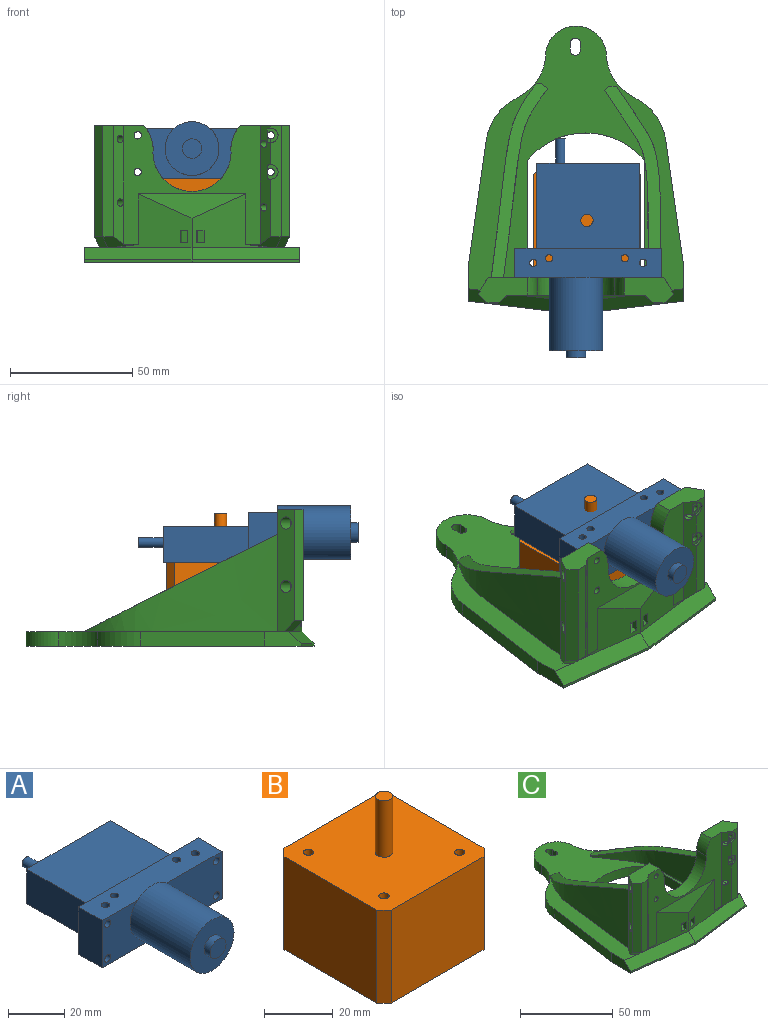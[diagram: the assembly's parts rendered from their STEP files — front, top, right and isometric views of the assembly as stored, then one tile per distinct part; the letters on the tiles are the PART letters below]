
ASSEMBLY  parts=3 mates=2
PART A: 25 faces, bbox 60x89.8x23.3 mm
  f0: plane 20.5x11.8mm, normal (1,0,0), area 241.9mm2, adj f1,f7,f8,f9
  f1: plane 60x20.5mm, normal (0,1,0), area 571.7mm2, adj f0,f2,f8,f9,f10,f11,f12,f13
  f2: plane 20.5x11.8mm, normal (-1,0,0), area 241.9mm2, adj f1,f7,f8,f9
  f3: cylinder r=1.5mm len=20.5mm, axis (0,0,-1), area 193.2mm2, adj f8,f9
  f4: cylinder r=1.5mm len=20.5mm, axis (0,0,-1), area 193.2mm2, adj f8,f9
  f5: cylinder r=1.5mm len=20.5mm, axis (0,0,-1), area 193.2mm2, adj f8,f9
  f6: cylinder r=1.5mm len=20.5mm, axis (0,0,-1), area 193.2mm2, adj f8,f9
  f7: plane 60x20.5mm, normal (0,-1,0), area 850.3mm2, adj f0,f2,f8,f9,f10,f11,f12,f13
  f8: plane 60x11.8mm, normal (0,0,1), area 679.7mm2, adj f0,f1,f2,f3,f4,f5,f6,f7
  f9: plane 60x46.8mm, normal (0,0,-1), area 2149.7mm2, adj f0,f1,f2,f3,f4,f5,f6,f7
  f10: cylinder r=1.5mm len=11.8mm, axis (0,1,0), area 111.2mm2, adj f1,f7
  f11: cylinder r=1.5mm len=11.8mm, axis (0,1,0), area 111.2mm2, adj f1,f7
  f12: cylinder r=1.5mm len=11.8mm, axis (0,1,0), area 111.2mm2, adj f1,f7
  f13: cylinder r=1.5mm len=11.8mm, axis (0,1,0), area 111.2mm2, adj f1,f7
  f14: plane 14.75x2.84mm, normal (0,1,0), area 28.7mm2, adj f8,f15
  f15: cylinder r=11mm len=30mm, axis (0,1,0), area 2073.5mm2, adj f7,f14,f16
  f16: plane 22x22mm, normal (0,-1,0), area 329.9mm2, adj f15,f17
  f17: cylinder r=4mm len=8mm, axis (0,1,0), area 75.4mm2, adj f16,f18
  f18: plane 8x8mm, normal (0,-1,0), area 50.3mm2, adj f17
  f19: plane 35x15mm, normal (1,0,0), area 525mm2, adj f1,f9,f21,f22
  f20: plane 35x15mm, normal (-1,0,0), area 525mm2, adj f1,f9,f21,f22
  f21: plane 42x35mm, normal (0,0,1), area 1470mm2, adj f1,f19,f20,f22
  f22: plane 42x15mm, normal (0,1,0), area 617.4mm2, adj f9,f19,f20,f21,f23
  f23: cylinder r=2mm len=10mm, axis (0,-1,0), area 125.7mm2, adj f22,f24
  f24: plane 4x4mm, normal (0,1,0), area 12.6mm2, adj f23
PART B: 20 faces, bbox 44x44x53 mm
  f0: plane 38x33mm, normal (1,0,0), area 1254mm2, adj f4,f5,f10,f11
  f1: plane 38x33mm, normal (0,1,0), area 1254mm2, adj f4,f5,f9,f11
  f2: plane 38x33mm, normal (-1,0,0), area 1254mm2, adj f4,f5,f8,f9
  f3: plane 38x33mm, normal (0,-1,0), area 1254mm2, adj f4,f5,f8,f10
  f4: plane 44x44mm, normal (0,0,1), area 1870.1mm2, adj f0,f1,f2,f3,f6,f8,f9,f10
  f5: plane 44x44mm, normal (0,0,-1), area 1918mm2, adj f0,f1,f2,f3,f8,f9,f10,f11
  f6: cylinder r=2.5mm len=20mm, axis (0,0,-1), area 314.2mm2, adj f4,f7
  f7: plane 5x5mm, normal (0,0,1), area 19.6mm2, adj f6
  f8: plane 33x3mm, normal (-0.71,-0.71,0), area 140mm2, adj f2,f3,f4,f5
  f9: plane 33x3mm, normal (-0.71,0.71,0), area 140mm2, adj f1,f2,f4,f5
  f10: plane 33x3mm, normal (0.71,-0.71,0), area 140mm2, adj f0,f3,f4,f5
  f11: plane 33x3mm, normal (0.71,0.71,0), area 140mm2, adj f0,f1,f4,f5
  f12: cylinder r=1.5mm len=10mm, axis (0,0,1), area 94.2mm2, adj f4,f13
  f13: plane 3x3mm, normal (0,0,1), area 7.1mm2, adj f12
  f14: cylinder r=1.5mm len=10mm, axis (0,0,1), area 94.2mm2, adj f4,f15
  f15: plane 3x3mm, normal (0,0,1), area 7.1mm2, adj f14
  f16: cylinder r=1.5mm len=10mm, axis (0,0,1), area 94.2mm2, adj f4,f17
  f17: plane 3x3mm, normal (0,0,1), area 7.1mm2, adj f16
  f18: cylinder r=1.5mm len=10mm, axis (0,0,1), area 94.2mm2, adj f4,f19
  f19: plane 3x3mm, normal (0,0,1), area 7.1mm2, adj f18
PART C: 82 faces, bbox 88.2x118.2x56.2 mm
  f0: cylinder r=1.5mm len=9.5mm, axis (0,1,0), area 82.8mm2, adj f14,f60,f61,f79
  f1: plane 45.5x4.5mm, normal (0,-1,0), area 173.5mm2, adj f39,f40,f42,f43,f78,f80
  f2: cylinder r=1.5mm len=9.5mm, axis (0,1,0), area 89.5mm2, adj f14,f81
  f3: plane 32.81x22mm, normal (0.12,-0.99,0), area 369.7mm2, adj f30,f31,f38,f43,f47,f70,f71,f73
  f4: extruded ~77.41x40mm, area 1610mm2, adj f5,f7,f14,f69
  f5: plane 2.52x1.91mm, normal (0.6,0.8,0), area 1.5mm2, adj f4,f7,f69
  f6: extruded ~79.32x40mm, area 1608.4mm2, adj f7,f14,f69
  f7: plane 108.75x88mm, normal (0,0,1), area 3048.4mm2, adj f4,f5,f6,f9,f10,f11,f12,f13
  f8: plane 20.17x10.5mm, normal (0,0,1), area 159.1mm2, adj f14,f34,f35,f36,f37,f38,f52
  f9: plane 6x2.8mm, normal (-1,0,0), area 16.8mm2, adj f7,f10,f27,f28
  f10: cylinder r=2.1mm len=6mm, axis (0,0,-1), area 39.6mm2, adj f7,f9,f11,f28
  f11: plane 6x2.8mm, normal (1,0,0), area 16.8mm2, adj f7,f10,f27,f28
  f12: cylinder r=31.33mm len=48mm, axis (0,0,-1), area 328.1mm2, adj f7,f13,f25,f28
  f13: plane 48x6mm, normal (-1,0,0), area 288mm2, adj f7,f12,f14,f28
  f14: plane 72.02x56.02mm, normal (0,1,0), area 2746.9mm2, adj f0,f2,f4,f6,f7,f8,f13,f25
  f15: plane 50.8x7.22mm, normal (0.99,0.14,0), area 307.9mm2, adj f7,f16,f26,f28
  f16: cylinder r=23.08mm len=17.52mm, axis (0,0,-1), area 135.4mm2, adj f7,f15,f17,f28
  f17: cylinder r=20.78mm len=16.02mm, axis (0,0,-1), area 123.4mm2, adj f7,f16,f18,f28
  f18: cylinder r=12.5mm len=25mm, axis (0,0,-1), area 245.8mm2, adj f7,f17,f19,f28
  f19: cylinder r=20.78mm len=16.02mm, axis (0,0,-1), area 123.4mm2, adj f7,f18,f20,f28
  f20: cylinder r=23.08mm len=17.52mm, axis (0,0,-1), area 135.4mm2, adj f7,f19,f21,f28
  f21: plane 50.8x7.22mm, normal (-0.99,0.14,0), area 307.9mm2, adj f7,f20,f22,f28
  f22: plane 15x6mm, normal (-1,0,0), area 77.4mm2, adj f7,f21,f23,f28,f29
  f23: plane 44x5.32mm, normal (-0.12,-0.99,0), area 44.3mm2, adj f22,f24,f28,f29
  f24: plane 44x5.32mm, normal (0.12,-0.99,0), area 44.3mm2, adj f23,f26,f28,f30
  f25: plane 48x6mm, normal (1,0,0), area 288mm2, adj f7,f12,f14,f28
  f26: plane 15x6mm, normal (1,0,0), area 77.4mm2, adj f7,f15,f24,f28,f30
  f27: cylinder r=2.1mm len=6mm, axis (0,0,-1), area 39.6mm2, adj f7,f9,f11,f28
  f28: plane 118x88mm, normal (0,0,-1), area 4882.9mm2, adj f9,f10,f11,f12,f13,f14,f15,f16
  f29: plane 44x10.35mm, normal (-0.08,-0.7,0.71), area 313.4mm2, adj f7,f22,f23,f30,f31,f32
  f30: plane 44x10.35mm, normal (0.08,-0.7,0.71), area 313.4mm2, adj f3,f7,f24,f26,f29,f33
  f31: plane 32.81x22mm, normal (-0.12,-0.99,0), area 370.2mm2, adj f3,f29,f38,f45,f47,f72,f73,f74
  f32: plane 2.04x0.25mm, normal (0,0,-1), area 0.2mm2, adj f29,f45,f46
  f33: plane 2.04x0.25mm, normal (0,0,-1), area 0.2mm2, adj f30,f43,f44
  f34: plane 50x6.93mm, normal (-0.87,0.5,0), area 350.2mm2, adj f7,f8,f14,f35,f46,f55,f58
  f35: plane 45.5x3.57mm, normal (-0.71,-0.7,0), area 227.5mm2, adj f8,f34,f36,f46
  f36: plane 45.5x4.5mm, normal (0,-1,0), area 204.7mm2, adj f8,f35,f37,f45
  f37: plane 48.7x4mm, normal (0.62,-0.78,0), area 226.1mm2, adj f8,f36,f38,f45,f53,f56
  f38: plane 56x48.7mm, normal (0,-1,0), area 1024.3mm2, adj f3,f8,f31,f37,f39,f42,f43,f45
  f39: plane 48.95x4.25mm, normal (-0.62,-0.78,0), area 207.8mm2, adj f1,f38,f42,f43,f59,f62,f78,f79
  f40: plane 45.5x3.57mm, normal (0.71,-0.7,0), area 227.5mm2, adj f1,f41,f42,f44
  f41: plane 50x6.93mm, normal (0.87,0.5,0), area 350.2mm2, adj f7,f14,f40,f42,f44,f61,f64
  f42: plane 20.17x10.5mm, normal (0,0,1), area 159.1mm2, adj f1,f14,f38,f39,f40,f41,f51
  f43: plane 14.46x4.5mm, normal (0,-0.71,-0.71), area 40.1mm2, adj f1,f3,f33,f38,f39,f44
  f44: plane 7.62x5.39mm, normal (0.5,-0.49,-0.71), area 29.8mm2, adj f7,f33,f40,f41,f43
  f45: plane 14.46x4.5mm, normal (0,-0.71,-0.71), area 40.1mm2, adj f31,f32,f36,f37,f38,f46
  f46: plane 7.62x5.39mm, normal (-0.5,-0.49,-0.71), area 29.8mm2, adj f7,f32,f34,f35,f45
  f47: plane 44.09x9.94mm, normal (0,-0.97,0.26), area 226.9mm2, adj f3,f31,f38
  f48: cylinder r=1.5mm len=7.3mm, axis (0,1,0), area 68.8mm2, adj f14,f38
  f49: cylinder r=1.5mm len=7.3mm, axis (0,1,0), area 68.8mm2, adj f14,f38
  f50: cylinder r=16mm len=32mm, axis (0,1,0), area 390.3mm2, adj f14,f38,f51,f52
  f51: cylinder r=14mm len=9.4mm, axis (0,1,0), area 76.1mm2, adj f14,f38,f42,f50
  f52: cylinder r=14mm len=9.4mm, axis (0,1,0), area 76.1mm2, adj f8,f14,f38,f50
  f53: cylinder r=1.5mm len=3.86mm, axis (-0.87,0.5,0), area 18.1mm2, adj f37,f54
  f54: plane 5x4.33mm, normal (-0.87,0.5,0), area 12.6mm2, adj f53,f55
  f55: cylinder r=2.5mm len=9.43mm, axis (-0.87,0.5,0), area 125.7mm2, adj f34,f54
  f56: cylinder r=1.5mm len=3.86mm, axis (-0.87,0.5,0), area 18.1mm2, adj f37,f57
  f57: plane 5x4.33mm, normal (-0.87,0.5,0), area 12.6mm2, adj f56,f58
  f58: cylinder r=2.5mm len=9.43mm, axis (-0.87,0.5,0), area 125.7mm2, adj f34,f57
  f59: cylinder r=1.5mm len=3.85mm, axis (0.87,0.5,0), area 18.1mm2, adj f39,f60
  f60: plane 5.09x4.42mm, normal (0.87,0.5,0), area 12.4mm2, adj f0,f59,f61,f78,f79
  f61: cylinder r=2.5mm len=9.43mm, axis (0.87,0.5,0), area 119.2mm2, adj f0,f41,f60,f78,f79
  f62: cylinder r=1.5mm len=3.85mm, axis (0.87,0.5,0), area 18.1mm2, adj f39,f63
  f63: plane 5x4.33mm, normal (0.87,0.5,0), area 12.6mm2, adj f62,f64
  f64: cylinder r=2.5mm len=9.43mm, axis (0.87,0.5,0), area 125.7mm2, adj f41,f63
  f65: extruded ~76.59x27mm, area 1079mm2, adj f7,f14,f67,f68
  f66: extruded ~78.32x27mm, area 1076.6mm2, adj f7,f14,f68
  f67: plane 1.73x1.58mm, normal (-0.74,0.67,0), area 0.7mm2, adj f7,f65,f68
  f68: plane 78.32x27mm, normal (0,0.33,0.95), area 437.4mm2, adj f7,f14,f65,f66,f67
  f69: plane 79.32x40mm, normal (0,0.45,0.89), area 459.9mm2, adj f4,f5,f6,f7,f14
  f70: plane 5x3.79mm, normal (-0.99,0.12,0), area 19.1mm2, adj f3,f73,f75,f76
  f71: plane 5x2.04mm, normal (0.99,-0.12,0), area 10.3mm2, adj f3,f73,f75,f77
  f72: plane 5x4.96mm, normal (0.99,-0.12,0), area 25mm2, adj f31,f73,f75,f76
  f73: plane 10.2x5.32mm, normal (0,0,1), area 36.7mm2, adj f3,f31,f70,f71,f72,f74,f76,f77
  f74: plane 5x2.48mm, normal (-0.99,0.12,0), area 12.5mm2, adj f31,f73,f75,f77
  f75: plane 10.2x5.32mm, normal (0,0,-1), area 36.7mm2, adj f3,f31,f70,f71,f72,f74,f76,f77
  f76: plane 9.6x5mm, normal (-0.12,-0.99,0), area 48.3mm2, adj f70,f72,f73,f75
  f77: plane 5x3.64mm, normal (0.12,0.99,0), area 18.3mm2, adj f71,f73,f74,f75
  f78: cylinder r=3mm len=6mm, axis (0,-1,0), area 11.2mm2, adj f1,f39,f60,f61,f79
  f79: plane 6.02x4.52mm, normal (0,-1,0), area 15.6mm2, adj f0,f39,f60,f61,f78
  f80: cylinder r=3mm len=6mm, axis (0,-1,0), area 11.2mm2, adj f1,f39,f81
  f81: plane 6x4.5mm, normal (0,-1,0), area 15.7mm2, adj f2,f39,f80
PLACE A t=(0.05,-3.48,-11.68)mm
PLACE B t=(-0.45,13.92,-44.68)mm fixed
PLACE C t=(-4.95,-4.06,-45.93)mm
MATE fastened A.f10 <-> C.f49  axis (0,-1,0) through (-27.2,-9.38,6.07)mm
MATE fastened B.f16 <-> A.f6  axis (0,0,1) through (15.05,-1.58,-11.68)mm
